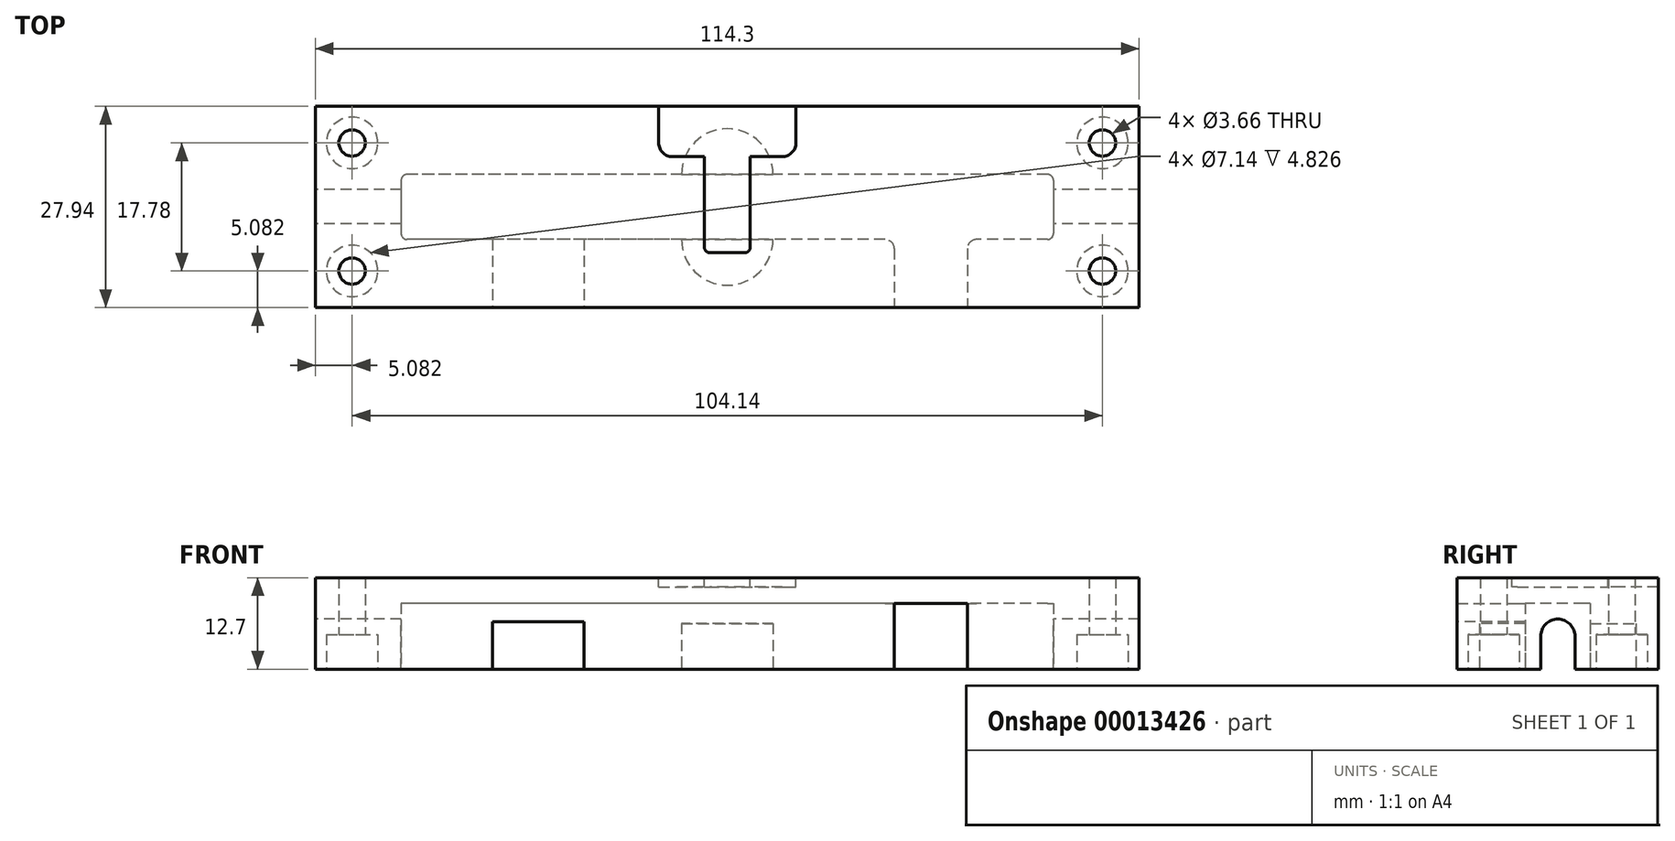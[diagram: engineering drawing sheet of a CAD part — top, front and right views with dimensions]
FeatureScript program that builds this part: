
annotation { "Feature Type Name" : "Feature", "Feature Type Description" : "" }
export const myFeature = defineFeature(function(context is Context, id is Id, definition is map)
    precondition{}
    {
        {
            var Q0;
            Q0=qCreatedBy(makeId("Top.planeOp"),FACE);
            var sketch = newSketch(context, id + "F0", { "sketchPlane" : qUnion([Q0])});
            skLineSegment(sketch, "E0.bottom", {"start": v(-44.98, -11.5) * mm, "end": v(69.32, -11.5) * mm});
            skLineSegment(sketch, "E0.top", {"start": v(-44.98, 16.43) * mm, "end": v(69.32, 16.43) * mm});
            skLineSegment(sketch, "E0.left", {"start": v(-44.98, -11.5) * mm, "end": v(-44.98, 16.43) * mm});
            skLineSegment(sketch, "E0.right", {"start": v(69.32, -11.5) * mm, "end": v(69.32, 16.43) * mm});
            skSolve(sketch);
        }
        {
            var Q0;
            Q0=makeQuery(id+"F0.imprint","IMPRINT",FACE,{"disambiguationData":[TD([[makeQuery(id+"F0.imprint","IMPRINT",EDGE,{"derivedFrom":sQuery(id+"F0.wireOp",EDGE,"E0.bottom")}),1.0]])]});
            extrude(context, id + "F1", {"entities" : qUnion([Q0]), "depth" : 12.7 * mm});
        }
        {
            var Q0;
            Q0=makeQuery(id+"F1.opExtrude","CAP_FACE",FACE,{"disambiguationData":[OSD([sQuery(id+"F0.wireOp",EDGE,"E0.bottom"),sQuery(id+"F0.wireOp",EDGE,"E0.top"),sQuery(id+"F0.wireOp",EDGE,"E0.left"),sQuery(id+"F0.wireOp",EDGE,"E0.right")])],"isStart":true});
            var sketch = newSketch(context, id + "F2", { "sketchPlane" : qUnion([Q0])});
            skLineSegment(sketch, "E1.bottom", {"start": v(56.62, -6.97) * mm, "end": v(-32.28, -6.97) * mm});
            skLineSegment(sketch, "E1.top", {"start": v(56.62, 2.05) * mm, "end": v(-32.28, 2.05) * mm});
            skLineSegment(sketch, "E1.left", {"start": v(57.43, -6.16) * mm, "end": v(57.43, 1.23) * mm});
            skLineSegment(sketch, "E1.right", {"start": v(-33.1, -6.16) * mm, "end": v(-33.1, 1.23) * mm});
            skPoint(sketch, "E2.visualSharp", {"position": v(57.43, -6.97) * mm});
            skArc(sketch, "E2.filletArc", {"start": v(56.62, -6.97) * mm, "mid": v(57.2, -6.73) * mm, "end": v(57.43, -6.16) * mm});
            skPoint(sketch, "E3.visualSharp", {"position": v(57.43, 2.05) * mm});
            skArc(sketch, "E3.filletArc", {"start": v(57.43, 1.23) * mm, "mid": v(57.2, 1.8) * mm, "end": v(56.62, 2.05) * mm});
            skPoint(sketch, "E4.visualSharp", {"position": v(-33.1, -6.97) * mm});
            skArc(sketch, "E4.filletArc", {"start": v(-33.1, -6.16) * mm, "mid": v(-32.85, -6.73) * mm, "end": v(-32.28, -6.97) * mm});
            skPoint(sketch, "E5.visualSharp", {"position": v(-33.1, 2.05) * mm});
            skArc(sketch, "E5.filletArc", {"start": v(-32.28, 2.05) * mm, "mid": v(-32.85, 1.8) * mm, "end": v(-33.1, 1.23) * mm});
            skSolve(sketch);
        }
        {
            var Q0;
            Q0 = qSketchRegion(id + "F2", true);
            extrude(context, id + "F3", {"entities" : qUnion([Q0]), "operationType" : NewBodyOperationType.REMOVE, "oppositeDirection" : true, "depth" : 9.14 * mm});
        }
        {
            var Q0;
            Q0=makeQuery(id+"F1.opExtrude","CAP_FACE",FACE,{"disambiguationData":[OSD([sQuery(id+"F0.wireOp",EDGE,"E0.bottom"),sQuery(id+"F0.wireOp",EDGE,"E0.top"),sQuery(id+"F0.wireOp",EDGE,"E0.left"),sQuery(id+"F0.wireOp",EDGE,"E0.right")])],"isStart":false});
            var sketch = newSketch(context, id + "F4", { "sketchPlane" : qUnion([Q0])});
            skLineSegment(sketch, "E6", {"start": v(21.7, 16.43) * mm, "end": v(21.7, 11.35) * mm});
            skLineSegment(sketch, "E7", {"start": v(19.8, 9.45) * mm, "end": v(15.35, 9.45) * mm});
            skPoint(sketch, "E8.visualSharp", {"position": v(21.7, 9.45) * mm});
            skArc(sketch, "E8.filletArc", {"start": v(19.8, 9.45) * mm, "mid": v(21.14, 10) * mm, "end": v(21.7, 11.35) * mm});
            skLineSegment(sketch, "E9", {"start": v(2.65, 11.35) * mm, "end": v(2.65, 16.43) * mm});
            skLineSegment(sketch, "E10", {"start": v(2.65, 16.43) * mm, "end": v(21.7, 16.43) * mm});
            skPoint(sketch, "E11.visualSharp", {"position": v(2.65, 9.45) * mm});
            skArc(sketch, "E11.filletArc", {"start": v(2.65, 11.35) * mm, "mid": v(3.2, 10) * mm, "end": v(4.55, 9.45) * mm});
            skLineSegment(sketch, "E12.bottom", {"start": v(14.58, -3.89) * mm, "end": v(9.76, -3.89) * mm});
            skLineSegment(sketch, "E12.left", {"start": v(15.35, -3.13) * mm, "end": v(15.35, 9.45) * mm});
            skLineSegment(sketch, "E12.right", {"start": v(9, -3.13) * mm, "end": v(9, 9.45) * mm});
            skPoint(sketch, "E13.visualSharp", {"position": v(15.35, -3.89) * mm});
            skArc(sketch, "E13.filletArc", {"start": v(14.58, -3.89) * mm, "mid": v(15.12, -3.66) * mm, "end": v(15.35, -3.13) * mm});
            skPoint(sketch, "E14.visualSharp", {"position": v(15.35, 9.45) * mm});
            skPoint(sketch, "E15.visualSharp", {"position": v(9, 9.45) * mm});
            skPoint(sketch, "E16.visualSharp", {"position": v(9, -3.89) * mm});
            skArc(sketch, "E16.filletArc", {"start": v(9, -3.13) * mm, "mid": v(9.22, -3.66) * mm, "end": v(9.76, -3.89) * mm});
            skLineSegment(sketch, "E17", {"start": v(9, 9.45) * mm, "end": v(9, 9.45) * mm});
            skLineSegment(sketch, "E18", {"start": v(15.35, 9.45) * mm, "end": v(15.35, 9.45) * mm});
            skLineSegment(sketch, "E19.trimOffspring", {"start": v(9, 9.45) * mm, "end": v(4.55, 9.45) * mm});
            skSolve(sketch);
        }
        {
            var Q0;
            Q0 = qSketchRegion(id + "F4", true);
            var Q1;
            Q1=makeQuery(id+"FXOkJv0ckkrfQTb_1.boolean.opBoolean","COPY",FACE,{"derivedFrom":makeQuery(id+"FXOkJv0ckkrfQTb_1.opExtrude","CAP_FACE",FACE,{"disambiguationData":[OSD([sQuery(id+"FNH8KqWSbUaVyww_1.wireOp",EDGE,"95eef0d6-668e-4bf6-a172-0342ca8e1830.bottom"),sQuery(id+"FNH8KqWSbUaVyww_1.wireOp",EDGE,"95eef0d6-668e-4bf6-a172-0342ca8e1830.top"),sQuery(id+"FNH8KqWSbUaVyww_1.wireOp",EDGE,"95eef0d6-668e-4bf6-a172-0342ca8e1830.left"),sQuery(id+"FNH8KqWSbUaVyww_1.wireOp",EDGE,"95eef0d6-668e-4bf6-a172-0342ca8e1830.right"),sQuery(id+"FNH8KqWSbUaVyww_1.wireOp",EDGE,"d7b8f0e6-89bf-4d90-9a0f-a7446f85b501.bottom"),sQuery(id+"FNH8KqWSbUaVyww_1.wireOp",EDGE,"d7b8f0e6-89bf-4d90-9a0f-a7446f85b501.top"),sQuery(id+"FNH8KqWSbUaVyww_1.wireOp",EDGE,"d7b8f0e6-89bf-4d90-9a0f-a7446f85b501.left"),sQuery(id+"FNH8KqWSbUaVyww_1.wireOp",EDGE,"d7b8f0e6-89bf-4d90-9a0f-a7446f85b501.right"),sQuery(id+"FNH8KqWSbUaVyww_1.wireOp",EDGE,"efd13bb3-fbc7-4de9-8f96-348dde713d37.filletArc"),sQuery(id+"FNH8KqWSbUaVyww_1.wireOp",EDGE,"7ac8e13b-5649-4a3d-91c6-297c25820bfb.filletArc"),sQuery(id+"FNH8KqWSbUaVyww_1.wireOp",EDGE,"2ec1616d-3554-4afe-808e-9cb3dce9970b.filletArc"),sQuery(id+"FNH8KqWSbUaVyww_1.wireOp",EDGE,"5c109569-0ffe-45b0-9409-798be332c4d6.filletArc")])],"isStart":false})});
            extrude(context, id + "F5", {"entities" : qUnion([Q0]), "operationType" : NewBodyOperationType.REMOVE, "oppositeDirection" : true, "endBoundEntity" : qUnion([Q1]), "depth" : 1.27 * mm});
        }
        {
            var Q0;
            Q0=makeQuery(id+"F1.opExtrude","SWEPT_FACE",FACE,{"disambiguationData":[OSD([sQuery(id+"F0.wireOp",EDGE,"E0.left")])]});
            var sketch = newSketch(context, id + "F6", { "sketchPlane" : qUnion([Q0])});
            skArc(sketch, "E20", {"start": v(-0.1, 4.57) * mm, "mid": v(-2.49, 6.95) * mm, "end": v(-4.87, 4.57) * mm});
            skLineSegment(sketch, "E21", {"start": v(-4.87, 4.57) * mm, "end": v(-4.87, 0) * mm});
            skLineSegment(sketch, "E22", {"start": v(-4.87, 0) * mm, "end": v(-0.1, 0) * mm});
            skLineSegment(sketch, "E23", {"start": v(-0.1, 0) * mm, "end": v(-0.1, 4.57) * mm});
            skSolve(sketch);
        }
        {
            var Q0;
            Q0 = qSketchRegion(id + "F6", true);
            extrude(context, id + "F7", {"entities" : qUnion([Q0]), "operationType" : NewBodyOperationType.REMOVE, "endBound" : BoundingType.THROUGH_ALL, "oppositeDirection" : true, "depth" : 25.4 * mm});
        }
        {
            var Q0;
            {var subQ0=sQuery(id+"F0.wireOp",EDGE,"E0.bottom");var subQ1=sQuery(id+"F0.wireOp",EDGE,"E0.left");var subQ2=sQuery(id+"F0.wireOp",EDGE,"E0.right");Q0=makeQuery(id+"F7.boolean.opBoolean","SPLIT",FACE,{"disambiguationData":[TD([makeQuery(id+"F1.opExtrude","SWEPT_FACE",FACE,{"disambiguationData":[OSD([subQ0])]})])],"derivedFrom":makeQuery(id+"F1.opExtrude","CAP_FACE",FACE,{"disambiguationData":[OSD([subQ0,sQuery(id+"F0.wireOp",EDGE,"E0.top"),subQ1,subQ2])],"isStart":true})});}
            var sketch = newSketch(context, id + "F8", { "sketchPlane" : qUnion([Q0])});
            skArc(sketch, "E24", {"start": v(18.52, 2.05) * mm, "mid": v(12.17, 8.4) * mm, "end": v(5.82, 2.05) * mm});
            skArc(sketch, "E25", {"start": v(5.82, -6.97) * mm, "mid": v(12.17, -13.32) * mm, "end": v(18.52, -6.97) * mm});
            skLineSegment(sketch, "E26", {"start": v(5.82, 2.05) * mm, "end": v(5.82, -6.97) * mm});
            skLineSegment(sketch, "E27", {"start": v(18.52, 2.05) * mm, "end": v(18.52, -6.97) * mm});
            skSolve(sketch);
        }
        {
            var Q0;
            Q0 = qSketchRegion(id + "F8", true);
            extrude(context, id + "F9", {"entities" : qUnion([Q0]), "operationType" : NewBodyOperationType.REMOVE, "oppositeDirection" : true, "depth" : 6.35 * mm});
        }
        {
            var Q0;
            {var subQ0=sQuery(id+"F0.wireOp",EDGE,"E0.bottom");var subQ1=sQuery(id+"F0.wireOp",EDGE,"E0.left");var subQ2=sQuery(id+"F0.wireOp",EDGE,"E0.right");Q0=makeQuery(id+"F7.boolean.opBoolean","SPLIT",FACE,{"disambiguationData":[TD([makeQuery(id+"F1.opExtrude","SWEPT_FACE",FACE,{"disambiguationData":[OSD([subQ0])]})])],"derivedFrom":makeQuery(id+"F1.opExtrude","CAP_FACE",FACE,{"disambiguationData":[OSD([subQ0,sQuery(id+"F0.wireOp",EDGE,"E0.top"),subQ1,subQ2])],"isStart":true})});}
            var sketch = newSketch(context, id + "F10", { "sketchPlane" : qUnion([Q0])});
            skArc(sketch, "E28", {"start": v(45.5, 3.32) * mm, "mid": v(45.87, 2.42) * mm, "end": v(46.77, 2.05) * mm});
            skArc(sketch, "E29.1.0.0", {"start": v(34.07, 2.05) * mm, "mid": v(34.96, 2.42) * mm, "end": v(35.34, 3.32) * mm});
            skLineSegment(sketch, "E29.direction1", {"start": v(46.77, 3.32) * mm, "end": v(34.07, 3.32) * mm, "construction": true});
            skLineSegment(sketch, "E30.top", {"start": v(45.5, 11.5) * mm, "end": v(35.34, 11.5) * mm});
            skLineSegment(sketch, "E30.left", {"start": v(45.5, 3.32) * mm, "end": v(45.5, 11.5) * mm});
            skLineSegment(sketch, "E30.right", {"start": v(35.34, 3.32) * mm, "end": v(35.34, 11.5) * mm});
            skLineSegment(sketch, "E31", {"start": v(46.77, 2.05) * mm, "end": v(34.07, 2.05) * mm});
            skSolve(sketch);
        }
        {
            var Q0;
            Q0 = qSketchRegion(id + "F10", true);
            var Q1;
            Q1=makeQuery(id+"F3.boolean.opBoolean","COPY",FACE,{"derivedFrom":makeQuery(id+"F3.opExtrude","CAP_FACE",FACE,{"disambiguationData":[OSD([sQuery(id+"F2.wireOp",EDGE,"E1.bottom"),sQuery(id+"F2.wireOp",EDGE,"E1.top"),sQuery(id+"F2.wireOp",EDGE,"E1.left"),sQuery(id+"F2.wireOp",EDGE,"E1.right"),sQuery(id+"F2.wireOp",EDGE,"E2.filletArc"),sQuery(id+"F2.wireOp",EDGE,"E3.filletArc"),sQuery(id+"F2.wireOp",EDGE,"E4.filletArc"),sQuery(id+"F2.wireOp",EDGE,"E5.filletArc")])],"isStart":false})});
            extrude(context, id + "F11", {"entities" : qUnion([Q0]), "operationType" : NewBodyOperationType.REMOVE, "endBound" : BoundingType.UP_TO_SURFACE, "oppositeDirection" : true, "endBoundEntityFace" : qUnion([Q1]), "depth" : 25.4 * mm});
        }
        {
            var Q0;
            {var subQ0=sQuery(id+"F0.wireOp",EDGE,"E0.bottom");var subQ1=sQuery(id+"F0.wireOp",EDGE,"E0.left");var subQ2=sQuery(id+"F0.wireOp",EDGE,"E0.right");var subQ7=makeQuery(id+"F1.opExtrude","SWEPT_FACE",FACE,{"disambiguationData":[OSD([subQ1])]});var subQ8=makeQuery(id+"F1.opExtrude","SWEPT_FACE",FACE,{"disambiguationData":[OSD([subQ0])]});Q0=makeQuery(id+"F11.boolean.opBoolean","SPLIT",FACE,{"disambiguationData":[TD([subQ7])],"derivedFrom":makeQuery(id+"F7.boolean.opBoolean","SPLIT",FACE,{"disambiguationData":[TD([subQ8])],"derivedFrom":makeQuery(id+"F1.opExtrude","CAP_FACE",FACE,{"disambiguationData":[OSD([subQ0,sQuery(id+"F0.wireOp",EDGE,"E0.top"),subQ1,subQ2])],"isStart":true})})});}
            var sketch = newSketch(context, id + "F12", { "sketchPlane" : qUnion([Q0])});
            skLineSegment(sketch, "E32.bottom", {"start": v(-7.7, 2.05) * mm, "end": v(-20.4, 2.05) * mm});
            skLineSegment(sketch, "E32.top", {"start": v(-7.7, 11.5) * mm, "end": v(-20.4, 11.5) * mm});
            skLineSegment(sketch, "E32.left", {"start": v(-7.7, 2.05) * mm, "end": v(-7.7, 11.5) * mm});
            skLineSegment(sketch, "E32.right", {"start": v(-20.4, 2.05) * mm, "end": v(-20.4, 11.5) * mm});
            skSolve(sketch);
        }
        {
            var Q0;
            Q0 = qSketchRegion(id + "F12", true);
            extrude(context, id + "F13", {"entities" : qUnion([Q0]), "operationType" : NewBodyOperationType.REMOVE, "oppositeDirection" : true, "depth" : 6.6 * mm});
        }
        {
            var Q0;
            {var subQ0=sQuery(id+"F0.wireOp",EDGE,"E0.top");var subQ1=sQuery(id+"F0.wireOp",EDGE,"E0.left");var subQ2=sQuery(id+"F0.wireOp",EDGE,"E0.right");Q0=makeQuery(id+"F7.boolean.opBoolean","SPLIT",FACE,{"disambiguationData":[TD([makeQuery(id+"F1.opExtrude","SWEPT_FACE",FACE,{"disambiguationData":[OSD([subQ0])]})])],"derivedFrom":makeQuery(id+"F1.opExtrude","CAP_FACE",FACE,{"disambiguationData":[OSD([sQuery(id+"F0.wireOp",EDGE,"E0.bottom"),subQ0,subQ1,subQ2])],"isStart":true})});}
            var sketch = newSketch(context, id + "F14", { "sketchPlane" : qUnion([Q0])});
            skPoint(sketch, "E33", {"position": v(64.24, -11.35) * mm});
            skPoint(sketch, "E34", {"position": v(64.24, 6.43) * mm});
            skPoint(sketch, "E35", {"position": v(-39.9, -11.35) * mm});
            skPoint(sketch, "E36", {"position": v(-39.9, 6.43) * mm});
            skSolve(sketch);
        }
        {
            var Q0;
            Q0=sQuery(id+"F14.wireOp",VERTEX,"E33");
            var Q1;
            Q1=sQuery(id+"F14.wireOp",VERTEX,"E34");
            var Q2;
            Q2=sQuery(id+"F14.wireOp",VERTEX,"E35");
            var Q3;
            Q3=sQuery(id+"F14.wireOp",VERTEX,"E36");
            var Q4;
            Q4=makeQuery(id+"FvrC87ADXBSDjqa_1.boolean.opBoolean","SPLIT",BODY,{"disambiguationData":[OD(0.0)],"derivedFrom":makeQuery(id+"F1.opExtrude","SWEPT_BODY",BODY,{"disambiguationData":[OSD([sQuery(id+"F0.wireOp",EDGE,"E0.bottom"),sQuery(id+"F0.wireOp",EDGE,"E0.top"),sQuery(id+"F0.wireOp",EDGE,"E0.left"),sQuery(id+"F0.wireOp",EDGE,"E0.right")])]})});
            hole(context, id + "F15", {"style" : HoleStyle.C_BORE, "holeDiameter" : 3.66 * mm, "cBoreDiameter" : 7.14 * mm, "cBoreDepth" : 4.83 * mm, "endStyle" : HoleEndStyle.THROUGH, "locations" : qUnion([Q0, Q1, Q2, Q3]), "scope" : qUnion([Q4])});
        }
    });
